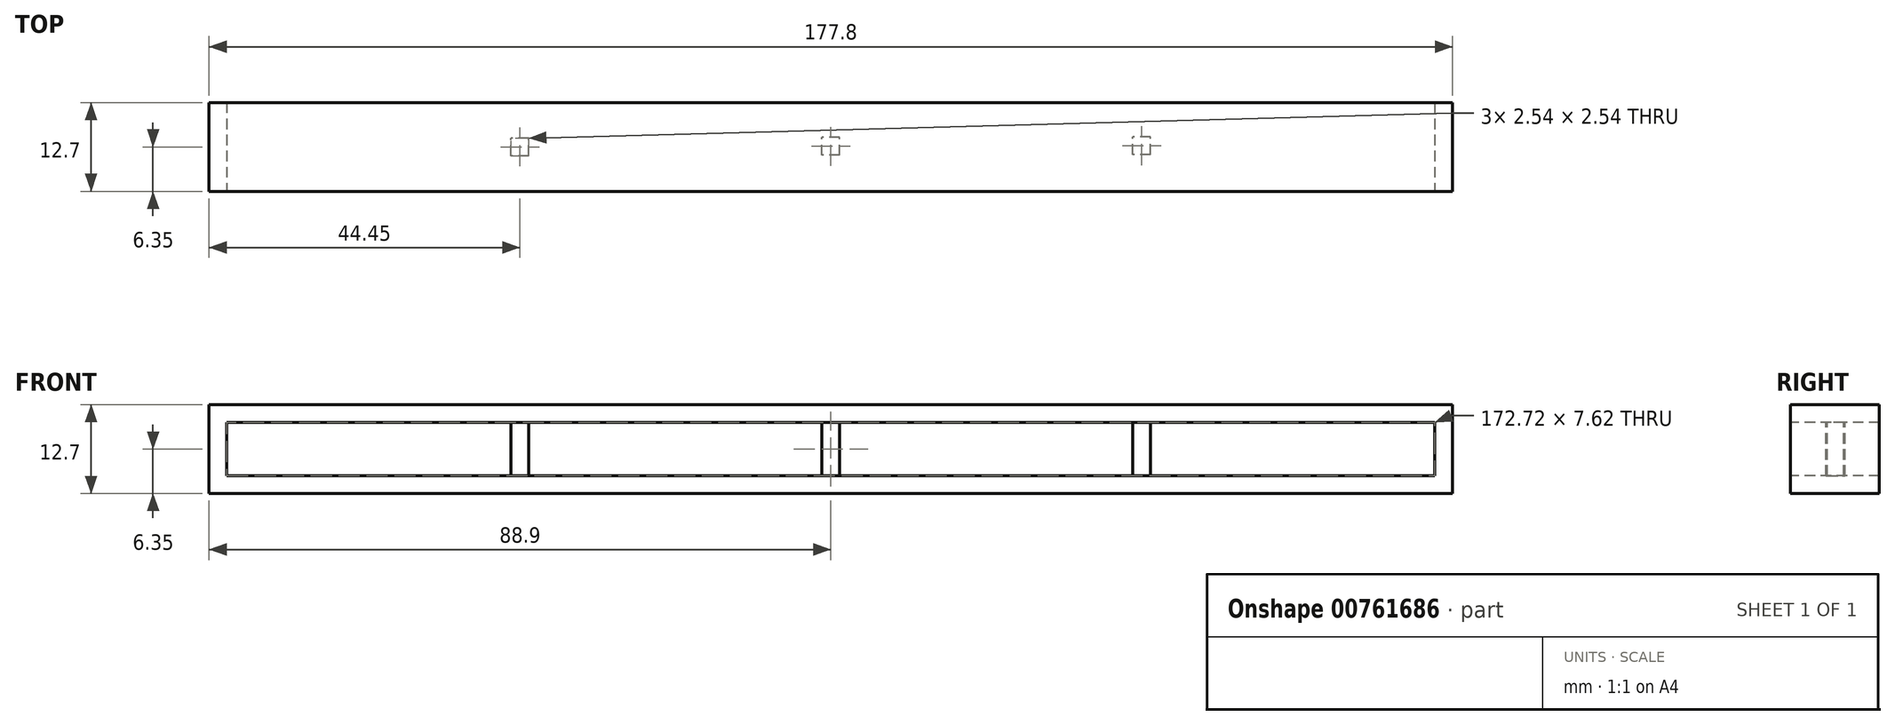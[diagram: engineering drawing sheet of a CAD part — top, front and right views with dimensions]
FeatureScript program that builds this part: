
annotation { "Feature Type Name" : "Feature", "Feature Type Description" : "" }
export const myFeature = defineFeature(function(context is Context, id is Id, definition is map)
    precondition{}
    {
        {
            var Q0;
            Q0=qCreatedBy(makeId("Right.planeOp"),FACE);
            var sketch = newSketch(context, id + "F0", { "sketchPlane" : qUnion([Q0])});
            skLineSegment(sketch, "E0.bottom", {"start": v(0, 0) * mm, "end": v(12.7, 0) * mm});
            skLineSegment(sketch, "E0.top", {"start": v(0, -2.54) * mm, "end": v(12.7, -2.54) * mm});
            skLineSegment(sketch, "E0.left", {"start": v(0, 0) * mm, "end": v(0, -2.54) * mm});
            skLineSegment(sketch, "E0.right", {"start": v(12.7, 0) * mm, "end": v(12.7, -2.54) * mm});
            skSolve(sketch);
        }
        {
            var Q0;
            Q0=qCreatedBy(makeId("Front.planeOp"),FACE);
            var sketch = newSketch(context, id + "F1", { "sketchPlane" : qUnion([Q0])});
            skLineSegment(sketch, "E1.bottom", {"start": v(0, 0) * mm, "end": v(177.8, 0) * mm});
            skLineSegment(sketch, "E1.top", {"start": v(0, -12.7) * mm, "end": v(177.8, -12.7) * mm});
            skLineSegment(sketch, "E1.left", {"start": v(0, 0) * mm, "end": v(0, -12.7) * mm});
            skLineSegment(sketch, "E1.right", {"start": v(177.8, 0) * mm, "end": v(177.8, -12.7) * mm});
            skSolve(sketch);
        }
        {
            var Q0;
            Q0=makeQuery(id+"F0.imprint","IMPRINT",FACE,{"disambiguationData":[TD([[makeQuery(id+"F0.imprint","IMPRINT",EDGE,{"derivedFrom":sQuery(id+"F0.wireOp",EDGE,"E0.bottom")}),-1.0]])]});
            var Q1;
            Q1=sQuery(id+"F1.wireOp",EDGE,"E1.bottom");
            var Q2;
            Q2=sQuery(id+"F1.wireOp",EDGE,"E1.right");
            var Q3;
            Q3=sQuery(id+"F1.wireOp",EDGE,"E1.top");
            var Q4;
            Q4=sQuery(id+"F1.wireOp",EDGE,"E1.left");
            sweep(context, id + "F2", {"profiles" : qUnion([Q0]), "path" : qUnion([Q1, Q2, Q3, Q4])});
        }
        {
            var Q0;
            Q0=qCreatedBy(makeId("Top.planeOp"),FACE);
            var sketch = newSketch(context, id + "F3", { "sketchPlane" : qUnion([Q0])});
            skLineSegment(sketch, "E2.bottom", {"start": v(45.72, 5.08) * mm, "end": v(43.18, 5.08) * mm});
            skLineSegment(sketch, "E2.top", {"start": v(45.72, 7.62) * mm, "end": v(43.18, 7.62) * mm});
            skLineSegment(sketch, "E2.left", {"start": v(45.72, 5.08) * mm, "end": v(45.72, 7.62) * mm});
            skLineSegment(sketch, "E2.right", {"start": v(43.18, 5.08) * mm, "end": v(43.18, 7.62) * mm});
            skPoint(sketch, "E2.middle", {"position": v(44.45, 6.35) * mm});
            skPoint(sketch, "E3.1.0.0", {"position": v(88.9, 6.44) * mm});
            skLineSegment(sketch, "E3.1.0.1", {"start": v(87.63, 5.17) * mm, "end": v(87.63, 7.7) * mm});
            skLineSegment(sketch, "E3.1.0.2", {"start": v(90.17, 5.17) * mm, "end": v(87.63, 5.17) * mm});
            skLineSegment(sketch, "E3.1.0.3", {"start": v(90.17, 5.17) * mm, "end": v(90.17, 7.7) * mm});
            skLineSegment(sketch, "E3.1.0.4", {"start": v(90.17, 7.7) * mm, "end": v(87.63, 7.7) * mm});
            skPoint(sketch, "E3.2.0.0", {"position": v(133.35, 6.53) * mm});
            skLineSegment(sketch, "E3.2.0.1", {"start": v(132.08, 5.26) * mm, "end": v(132.08, 7.8) * mm});
            skLineSegment(sketch, "E3.2.0.2", {"start": v(134.62, 5.26) * mm, "end": v(132.08, 5.26) * mm});
            skLineSegment(sketch, "E3.2.0.3", {"start": v(134.62, 5.26) * mm, "end": v(134.62, 7.8) * mm});
            skLineSegment(sketch, "E3.2.0.4", {"start": v(134.62, 7.8) * mm, "end": v(132.08, 7.8) * mm});
            skLineSegment(sketch, "E3.direction1", {"start": v(43.18, 5.08) * mm, "end": v(87.63, 5.17) * mm, "construction": true});
            skSolve(sketch);
        }
        {
            var Q0;
            Q0=makeQuery(id+"F3.imprint","IMPRINT",FACE,{"disambiguationData":[TD([[makeQuery(id+"F3.imprint","IMPRINT",EDGE,{"derivedFrom":sQuery(id+"F3.wireOp",EDGE,"E2.bottom")}),-1.0]])]});
            var Q1;
            Q1=makeQuery(id+"F3.imprint","IMPRINT",FACE,{"disambiguationData":[TD([[makeQuery(id+"F3.imprint","IMPRINT",EDGE,{"derivedFrom":sQuery(id+"F3.wireOp",EDGE,"E3.1.0.1")}),-1.0]])]});
            var Q2;
            Q2=makeQuery(id+"F3.imprint","IMPRINT",FACE,{"disambiguationData":[TD([[makeQuery(id+"F3.imprint","IMPRINT",EDGE,{"derivedFrom":sQuery(id+"F3.wireOp",EDGE,"E3.2.0.1")}),-1.0]])]});
            extrude(context, id + "F4", {"entities" : qUnion([Q0, Q1, Q2]), "operationType" : NewBodyOperationType.ADD, "oppositeDirection" : true, "depth" : 12.7 * mm, "offsetDistance" : 25.4 * mm});
        }
    });
